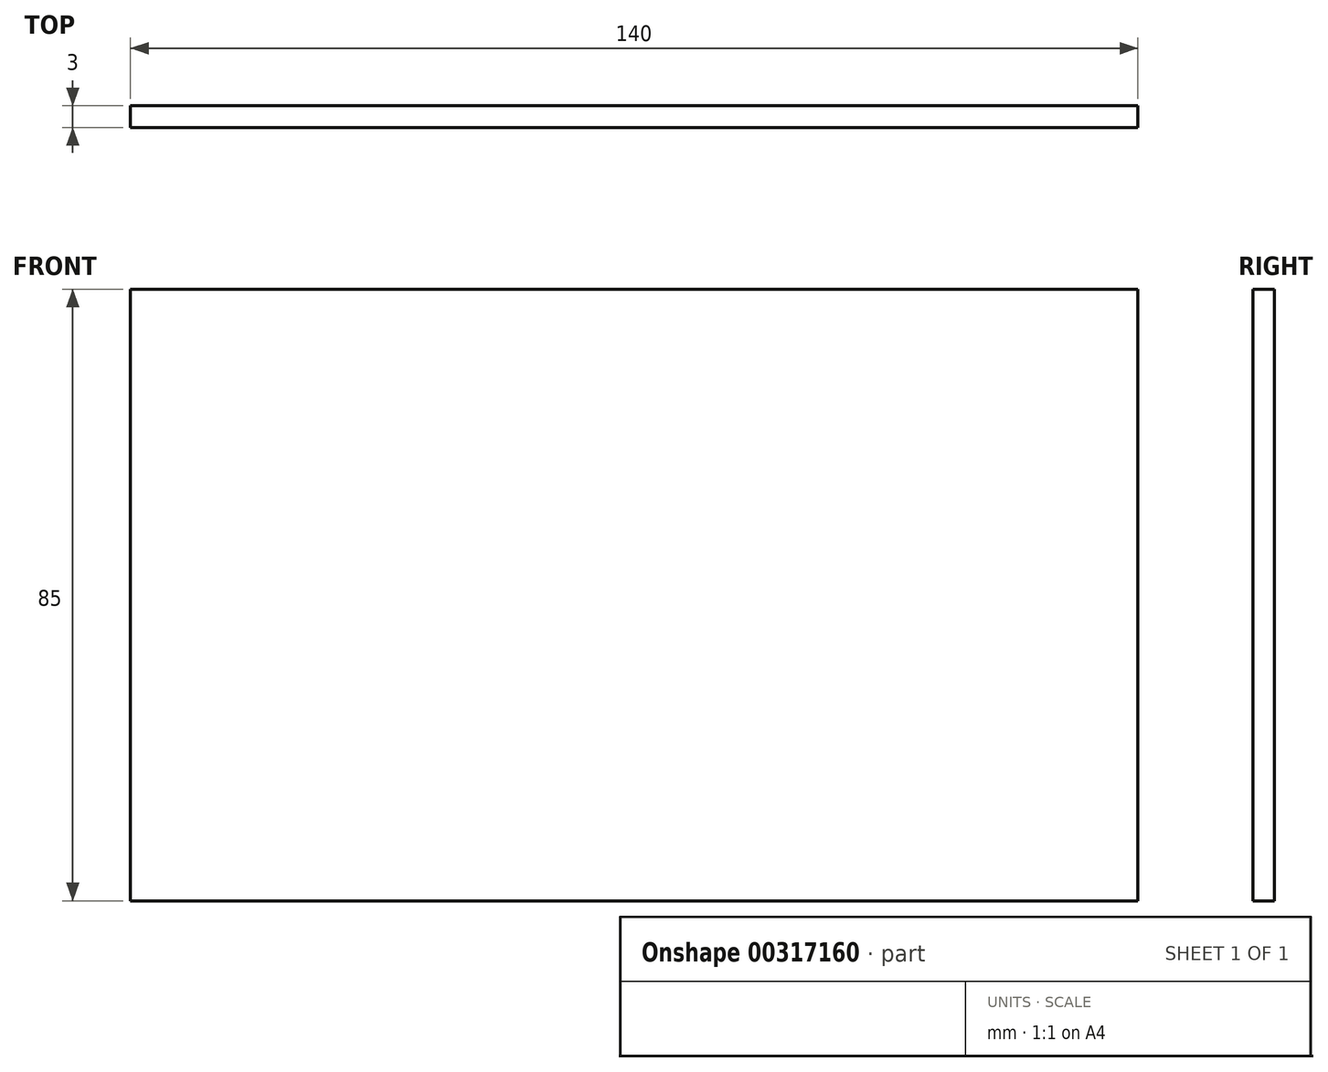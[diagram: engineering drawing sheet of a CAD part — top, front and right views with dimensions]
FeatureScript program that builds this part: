
annotation { "Feature Type Name" : "Feature", "Feature Type Description" : "" }
export const myFeature = defineFeature(function(context is Context, id is Id, definition is map)
    precondition{}
    {
        {
            var Q0;
            Q0=qCreatedBy(makeId("Front.planeOp"),FACE);
            var sketch = newSketch(context, id + "F0", { "sketchPlane" : qUnion([Q0])});
            skLineSegment(sketch, "E0.bottom", {"start": v(70, 42.5) * mm, "end": v(-70, 42.5) * mm});
            skLineSegment(sketch, "E0.top", {"start": v(70, -42.5) * mm, "end": v(-70, -42.5) * mm});
            skLineSegment(sketch, "E0.left", {"start": v(70, 42.5) * mm, "end": v(70, -42.5) * mm});
            skLineSegment(sketch, "E0.right", {"start": v(-70, 42.5) * mm, "end": v(-70, -42.5) * mm});
            skPoint(sketch, "E0.middle", {"position": v(0, 0) * mm});
            skSolve(sketch);
        }
        {
            var Q0;
            Q0=qSketchRegion(id+"F0",true);
            extrude(context, id + "F1", {"entities" : qUnion([Q0]), "depth" : 3 * mm});
        }
    });
